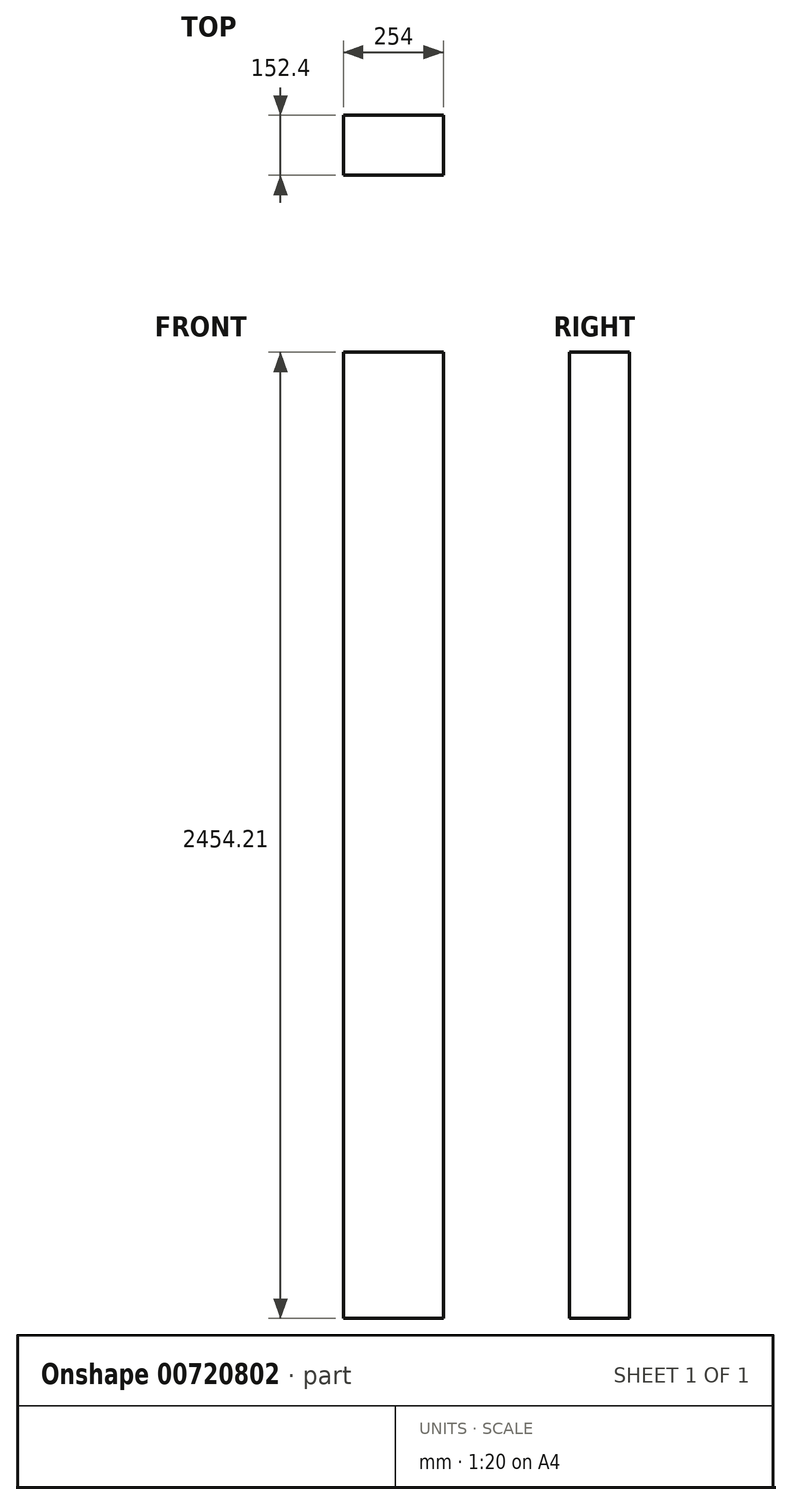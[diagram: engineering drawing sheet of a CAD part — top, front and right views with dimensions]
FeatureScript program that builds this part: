
annotation { "Feature Type Name" : "Feature", "Feature Type Description" : "" }
export const myFeature = defineFeature(function(context is Context, id is Id, definition is map)
    precondition{}
    {
        {
            var Q0;
            Q0=qCreatedBy(makeId("Top.planeOp"),FACE);
            var sketch = newSketch(context, id + "F0", { "sketchPlane" : qUnion([Q0])});
            skLineSegment(sketch, "E0.bottom", {"start": v(0, 0) * mm, "end": v(0, 0) * mm});
            skLineSegment(sketch, "E0.top", {"start": v(0, 0) * mm, "end": v(0, 0) * mm});
            skLineSegment(sketch, "E0.left", {"start": v(0, 0) * mm, "end": v(0, 0) * mm});
            skLineSegment(sketch, "E0.right", {"start": v(0, 0) * mm, "end": v(0, 0) * mm});
            skPoint(sketch, "E0.middle", {"position": v(0, 0) * mm});
            skLineSegment(sketch, "E1.bottom", {"start": v(-127, 76.2) * mm, "end": v(127, 76.2) * mm});
            skLineSegment(sketch, "E1.top", {"start": v(-127, -76.2) * mm, "end": v(127, -76.2) * mm});
            skLineSegment(sketch, "E1.left", {"start": v(-127, 76.2) * mm, "end": v(-127, -76.2) * mm});
            skLineSegment(sketch, "E1.right", {"start": v(127, 76.2) * mm, "end": v(127, -76.2) * mm});
            skLineSegment(sketch, "E2.left", {"start": v(-127, 0) * mm, "end": v(-127, 0) * mm});
            skLineSegment(sketch, "E2.right", {"start": v(127, 0) * mm, "end": v(127, 0) * mm});
            skSolve(sketch);
        }
        {
            var Q0;
            Q0=makeQuery(id+"F0.imprint","IMPRINT",FACE,{"disambiguationData":[TD([[makeQuery(id+"F0.imprint","IMPRINT",EDGE,{"derivedFrom":sQuery(id+"F0.wireOp",EDGE,"E1.bottom")}),-1.0]])]});
            extrude(context, id + "F1", {"entities" : qUnion([Q0]), "depth" : 2454.2 * mm, "offsetDistance" : 25.4 * mm});
        }
    });
